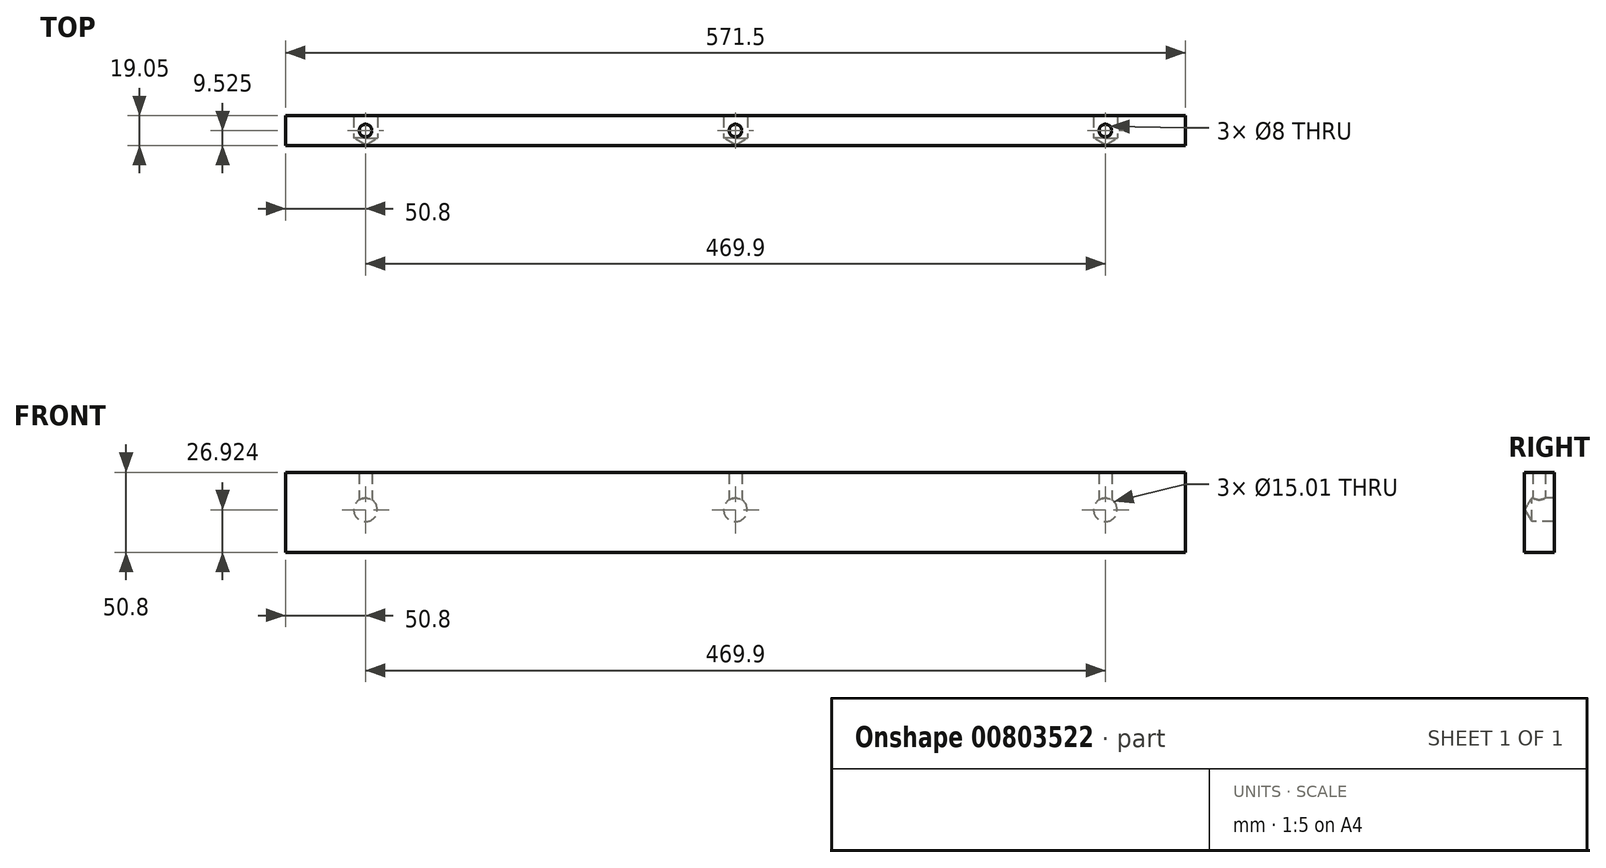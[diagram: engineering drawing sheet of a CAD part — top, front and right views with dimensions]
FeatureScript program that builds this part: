
annotation { "Feature Type Name" : "Feature", "Feature Type Description" : "" }
export const myFeature = defineFeature(function(context is Context, id is Id, definition is map)
    precondition{}
    {
        {
            var Q0;
            Q0=qCreatedBy(makeId("Front.planeOp"),FACE);
            var sketch = newSketch(context, id + "F0", { "sketchPlane" : qUnion([Q0])});
            skLineSegment(sketch, "E0.bottom", {"start": v(285.75, 25.4) * mm, "end": v(-285.75, 25.4) * mm});
            skLineSegment(sketch, "E0.top", {"start": v(285.75, -25.4) * mm, "end": v(-285.75, -25.4) * mm});
            skLineSegment(sketch, "E0.left", {"start": v(285.75, 25.4) * mm, "end": v(285.75, -25.4) * mm});
            skLineSegment(sketch, "E0.right", {"start": v(-285.75, 25.4) * mm, "end": v(-285.75, -25.4) * mm});
            skPoint(sketch, "E0.middle", {"position": v(0, 0) * mm});
            skSolve(sketch);
        }
        {
            var Q0;
            Q0=makeQuery(id+"F0.imprint","IMPRINT",FACE,{"disambiguationData":[TD([[makeQuery(id+"F0.imprint","IMPRINT",EDGE,{"derivedFrom":sQuery(id+"F0.wireOp",EDGE,"E0.bottom")}),1.0]])]});
            extrude(context, id + "F1", {"entities" : qUnion([Q0]), "depth" : 19.05 * mm, "offsetDistance" : 25.4 * mm});
        }
        {
            var Q0;
            Q0=makeQuery(id+"F1.opExtrude","CAP_FACE",FACE,{"disambiguationData":[OSD([sQuery(id+"F0.wireOp",EDGE,"E0.bottom"),sQuery(id+"F0.wireOp",EDGE,"E0.top"),sQuery(id+"F0.wireOp",EDGE,"E0.left"),sQuery(id+"F0.wireOp",EDGE,"E0.right")])],"isStart":true});
            var sketch = newSketch(context, id + "F2", { "sketchPlane" : qUnion([Q0])});
            skLineSegment(sketch, "E1", {"start": v(0, 25.4) * mm, "end": v(0, 1.52) * mm});
            skLineSegment(sketch, "E2", {"start": v(-285.75, 25.4) * mm, "end": v(-234.95, 25.4) * mm});
            skLineSegment(sketch, "E3", {"start": v(-234.95, 25.4) * mm, "end": v(-234.95, 1.52) * mm});
            skLineSegment(sketch, "E4", {"start": v(285.75, 25.4) * mm, "end": v(234.95, 25.4) * mm});
            skLineSegment(sketch, "E5", {"start": v(234.95, 25.4) * mm, "end": v(234.95, 1.52) * mm});
            skPoint(sketch, "E6", {"position": v(-234.95, 1.52) * mm});
            skPoint(sketch, "E7", {"position": v(0, 1.52) * mm});
            skPoint(sketch, "E8", {"position": v(234.95, 1.52) * mm});
            skSolve(sketch);
        }
        {
            var Q0;
            Q0=sQuery(id+"F2.wireOp",VERTEX,"E8");
            var Q1;
            Q1=sQuery(id+"F2.wireOp",VERTEX,"E7");
            var Q2;
            Q2=sQuery(id+"F2.wireOp",VERTEX,"E6");
            var Q3;
            Q3=makeQuery(id+"F1.opExtrude","SWEPT_BODY",BODY,{"disambiguationData":[OSD([sQuery(id+"F0.wireOp",EDGE,"E0.bottom"),sQuery(id+"F0.wireOp",EDGE,"E0.top"),sQuery(id+"F0.wireOp",EDGE,"E0.left"),sQuery(id+"F0.wireOp",EDGE,"E0.right")])]});
            hole(context, id + "F3", {"style" : HoleStyle.SIMPLE, "endStyle" : HoleEndStyle.BLIND, "holeDiameter" : 15 * mm, "majorDiameter" : 6.35 * mm, "holeDepth" : 14.22 * mm, "isTappedThrough" : true, "tappedDepth" : 12.7 * mm, "tapClearance" : 3, "startFromSketch" : true, "locations" : qUnion([Q0, Q1, Q2]), "scope" : qUnion([Q3])});
        }
        {
            var Q0;
            Q0=makeQuery(id+"F1.opExtrude","SWEPT_FACE",FACE,{"disambiguationData":[OSD([sQuery(id+"F0.wireOp",EDGE,"E0.bottom")])]});
            var sketch = newSketch(context, id + "F4", { "sketchPlane" : qUnion([Q0])});
            skLineSegment(sketch, "E9", {"start": v(-285.75, -9.53) * mm, "end": v(-234.95, -9.53) * mm});
            skLineSegment(sketch, "E10", {"start": v(285.75, -9.53) * mm, "end": v(234.95, -9.53) * mm});
            skLineSegment(sketch, "E11", {"start": v(0, 0) * mm, "end": v(0, -19.05) * mm});
            skPoint(sketch, "E12", {"position": v(-234.95, -9.53) * mm});
            skPoint(sketch, "E13", {"position": v(0, -9.53) * mm});
            skPoint(sketch, "E14", {"position": v(234.95, -9.53) * mm});
            skSolve(sketch);
        }
        {
            var Q0;
            Q0=sQuery(id+"F4.wireOp",VERTEX,"E12");
            var Q1;
            Q1=sQuery(id+"F4.wireOp",VERTEX,"E13");
            var Q2;
            Q2=sQuery(id+"F4.wireOp",VERTEX,"E14");
            var Q3;
            Q3=makeQuery(id+"F1.opExtrude","SWEPT_BODY",BODY,{"disambiguationData":[OSD([sQuery(id+"F0.wireOp",EDGE,"E0.bottom"),sQuery(id+"F0.wireOp",EDGE,"E0.top"),sQuery(id+"F0.wireOp",EDGE,"E0.left"),sQuery(id+"F0.wireOp",EDGE,"E0.right")])]});
            hole(context, id + "F5", {"style" : HoleStyle.SIMPLE, "endStyle" : HoleEndStyle.BLIND, "holeDiameter" : 8 * mm, "majorDiameter" : 6.35 * mm, "holeDepth" : 25.4 * mm, "isTappedThrough" : true, "tappedDepth" : 12.7 * mm, "tapClearance" : 3, "startFromSketch" : true, "locations" : qUnion([Q0, Q1, Q2]), "scope" : qUnion([Q3])});
        }
    });
